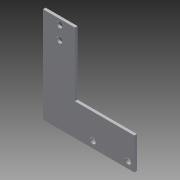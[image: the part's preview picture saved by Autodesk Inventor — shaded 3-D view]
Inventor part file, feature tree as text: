
AUTODESK INVENTOR PART (.ipt)
format: ipt  version: 2013 (Build 170138000, 138)  size: 148,480 bytes
history: native  units: in
note: dims shown in document units (in); Inventor stores cm internally (conversion verified against a paired STEP export)
features: sketch x6, other x5, reference x4, extrude x2, sheet_metal_op x1
ambient origin geometry x8: Origin, YZ Plane, XZ Plane, XY Plane, X Axis, Y Axis, Z Axis, Center Point
bodies: Solid1 (feature_tree)
feature tree (18):
  sheet_metal_op  "Face1"
  extrude  "Extrusion1"  Depth=1.5in
  extrude  "Extrusion3"  Depth=1.181in
  sketch  "Sketch1"  dims[d1=4.297in d2=1.5in]
  other  "Plate1"
  sketch  "Sketch8"  dims[d3=0.295in d4=1.181in]
  reference  "Reference1"
  reference  "Reference2"
  sketch  "Sketch10"  dims[d5=0.295in]
  sketch  "Sketch15"  dims[d8=0.125in]
  sketch  "Sketch16"  dims[d19=0.125in]
  reference  "Reference7"
  reference  "Reference8"
  sketch  "Sketch17"  dims[d20=0.0in d21=2.0in d22=2.053in d23=1.0in d24=0.0in d31=3.0in d32=0.0in d33=0.125in d34=0.0in d35=1.5in d36=0.125in d37=0.0in]
  other  "Cut1"
  other  "Cut4"
  other  "Cut5"
  other  "Definition1"
